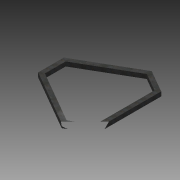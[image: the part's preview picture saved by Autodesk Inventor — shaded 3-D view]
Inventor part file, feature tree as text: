
AUTODESK INVENTOR PART (.ipt)
format: ipt  version: 2016 (Build 200138000, 138)  size: 88,064 bytes
history: native  units: in
note: dims shown in document units (in); Inventor stores cm internally (conversion verified against a paired STEP export)
features: extrude x1, sketch x1
ambient origin geometry x8: Origin, YZ Plane, XZ Plane, XY Plane, X Axis, Y Axis, Z Axis, Center Point
bodies: Body1 (feature_tree)
feature tree (2):
  extrude  "Extrusion7"  Depth=2.0in TaperAngle=0.0deg
  sketch  "Sketch1"  dims[d48=2.0in d49=2.0in d50=0.0in]
